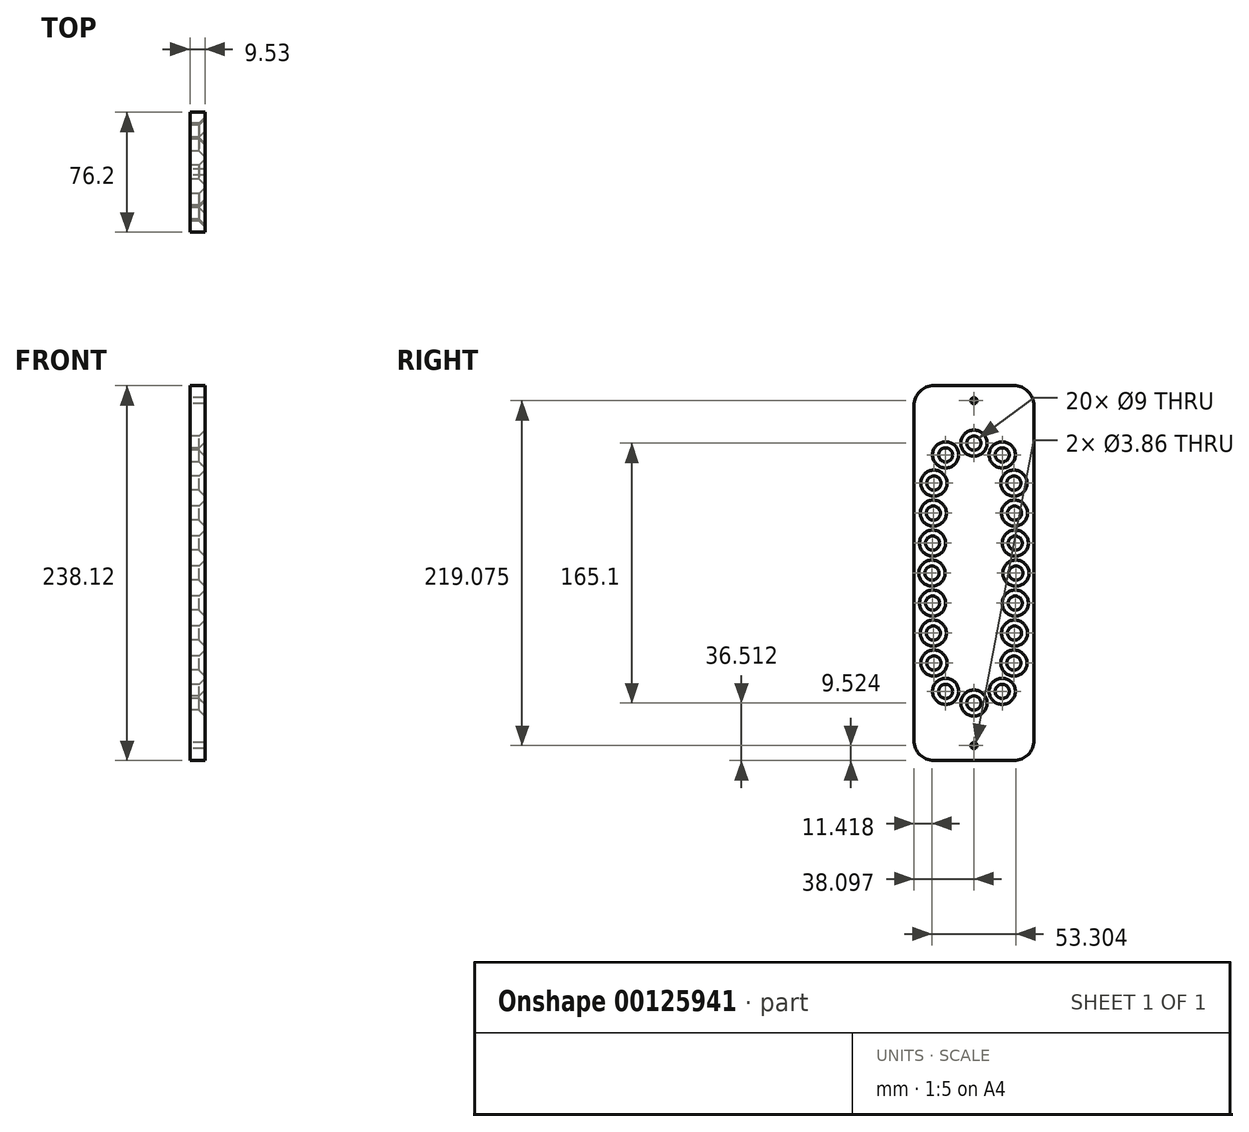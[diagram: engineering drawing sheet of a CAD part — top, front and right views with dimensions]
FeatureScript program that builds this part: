
annotation { "Feature Type Name" : "Feature", "Feature Type Description" : "" }
export const myFeature = defineFeature(function(context is Context, id is Id, definition is map)
    precondition{}
    {
        {
            var Q0;
            Q0=qCreatedBy(makeId("Right.planeOp"),FACE);
            var sketch = newSketch(context, id + "F0", { "sketchPlane" : qUnion([Q0])});
            skLineSegment(sketch, "E0", {"start": v(-38.07, 112.92) * mm, "end": v(-38.07, -99.8) * mm});
            skArc(sketch, "E1", {"start": v(-38.07, 112.92) * mm, "mid": v(-34.35, 121.9) * mm, "end": v(-25.37, 125.62) * mm});
            skLineSegment(sketch, "E2", {"start": v(-25.37, 125.62) * mm, "end": v(0.03, 125.62) * mm});
            skArc(sketch, "E3", {"start": v(-38.07, -99.8) * mm, "mid": v(-34.35, -108.78) * mm, "end": v(-25.37, -112.5) * mm});
            skLineSegment(sketch, "E4", {"start": v(-25.37, -112.5) * mm, "end": v(0.03, -112.5) * mm});
            skLineSegment(sketch, "E5.MirrorCS", {"start": v(25.43, -112.5) * mm, "end": v(0.03, -112.5) * mm});
            skArc(sketch, "E6.MirrorCS", {"start": v(38.13, -99.8) * mm, "mid": v(34.4, -108.78) * mm, "end": v(25.43, -112.5) * mm});
            skLineSegment(sketch, "E7.MirrorCS", {"start": v(25.43, 125.62) * mm, "end": v(0.03, 125.62) * mm});
            skLineSegment(sketch, "E8.MirrorCS", {"start": v(38.13, 112.92) * mm, "end": v(38.13, -99.8) * mm});
            skArc(sketch, "E9.MirrorCS", {"start": v(38.13, 112.92) * mm, "mid": v(34.4, 121.9) * mm, "end": v(25.43, 125.62) * mm});
            skCircle(sketch, "E10", {"center": v(0.03, 116.1) * mm, "radius": 1.93 * mm});
            skCircle(sketch, "E11", {"center": v(0.03, -102.98) * mm, "radius": 1.93 * mm});
            skLineSegment(sketch, "E12", {"start": v(0, -40.43) * mm, "end": v(0, 53.03) * mm, "construction": true});
            skCircle(sketch, "E13", {"center": v(0, 89.11) * mm, "radius": 4.5 * mm});
            skArc(sketch, "E14", {"start": v(-25.4, 63.71) * mm, "mid": v(0, 89.11) * mm, "end": v(25.4, 63.71) * mm, "construction": true});
            skLineSegment(sketch, "E15", {"start": v(-25.4, 63.71) * mm, "end": v(25.4, 63.71) * mm, "construction": true});
            skLineSegment(sketch, "E16", {"start": v(0, 63.71) * mm, "end": v(-17.96, 81.67) * mm, "construction": true});
            skCircle(sketch, "E17", {"center": v(-17.96, 81.67) * mm, "radius": 4.5 * mm});
            skCircle(sketch, "E18", {"center": v(-25.4, 63.71) * mm, "radius": 4.5 * mm});
            skLineSegment(sketch, "E19", {"start": v(-26.65, 6.56) * mm, "end": v(-25.4, 63.71) * mm, "construction": true});
            skCircle(sketch, "E20", {"center": v(-26.65, 6.56) * mm, "radius": 4.5 * mm});
            skCircle(sketch, "E21", {"center": v(-26.23, 25.61) * mm, "radius": 4.5 * mm});
            skCircle(sketch, "E22", {"center": v(-25.82, 44.66) * mm, "radius": 4.5 * mm});
            skCircle(sketch, "E23.MirrorC", {"center": v(26.65, 6.56) * mm, "radius": 4.5 * mm});
            skCircle(sketch, "E24.MirrorC", {"center": v(26.23, 25.61) * mm, "radius": 4.5 * mm});
            skCircle(sketch, "E25.MirrorC", {"center": v(25.82, 44.66) * mm, "radius": 4.5 * mm});
            skCircle(sketch, "E26.MirrorC", {"center": v(25.4, 63.71) * mm, "radius": 4.5 * mm});
            skCircle(sketch, "E27.MirrorC", {"center": v(17.96, 81.67) * mm, "radius": 4.5 * mm});
            skCircle(sketch, "E28.MirrorC", {"center": v(-26.23, -12.49) * mm, "radius": 4.5 * mm});
            skCircle(sketch, "E29.MirrorC", {"center": v(-25.82, -31.54) * mm, "radius": 4.5 * mm});
            skCircle(sketch, "E30.MirrorC", {"center": v(-25.4, -50.59) * mm, "radius": 4.5 * mm});
            skCircle(sketch, "E31.MirrorC", {"center": v(-17.96, -68.55) * mm, "radius": 4.5 * mm});
            skCircle(sketch, "E32.MirrorC", {"center": v(0, -75.99) * mm, "radius": 4.5 * mm});
            skCircle(sketch, "E33.MirrorC", {"center": v(17.96, -68.55) * mm, "radius": 4.5 * mm});
            skCircle(sketch, "E34.MirrorC", {"center": v(25.4, -50.59) * mm, "radius": 4.5 * mm});
            skCircle(sketch, "E35.MirrorC", {"center": v(25.82, -31.54) * mm, "radius": 4.5 * mm});
            skCircle(sketch, "E36.MirrorC", {"center": v(26.23, -12.49) * mm, "radius": 4.5 * mm});
            skSolve(sketch);
        }
        {
            var Q0;
            Q0 = qSketchRegion(id + "F0", true);
            extrude(context, id + "F1", {"entities" : qUnion([Q0]), "depth" : 9.52 * mm});
        }
        {
            var Q0;
            Q0=makeQuery(id+"F1.opExtrude","CAP_EDGE",EDGE,{"disambiguationData":[OSD([sQuery(id+"F0.wireOp",EDGE,"E13")])],"isStart":false});
            var Q1;
            Q1=makeQuery(id+"F1.opExtrude","CAP_EDGE",EDGE,{"disambiguationData":[OSD([sQuery(id+"F0.wireOp",EDGE,"E17")])],"isStart":false});
            var Q2;
            Q2=makeQuery(id+"F1.opExtrude","CAP_EDGE",EDGE,{"disambiguationData":[OSD([sQuery(id+"F0.wireOp",EDGE,"E18")])],"isStart":false});
            var Q3;
            Q3=makeQuery(id+"F1.opExtrude","CAP_EDGE",EDGE,{"disambiguationData":[OSD([sQuery(id+"F0.wireOp",EDGE,"E22")])],"isStart":false});
            var Q4;
            Q4=makeQuery(id+"F1.opExtrude","CAP_EDGE",EDGE,{"disambiguationData":[OSD([sQuery(id+"F0.wireOp",EDGE,"E21")])],"isStart":false});
            var Q5;
            Q5=makeQuery(id+"F1.opExtrude","CAP_EDGE",EDGE,{"disambiguationData":[OSD([sQuery(id+"F0.wireOp",EDGE,"E20")])],"isStart":false});
            var Q6;
            Q6=makeQuery(id+"F1.opExtrude","CAP_EDGE",EDGE,{"disambiguationData":[OSD([sQuery(id+"F0.wireOp",EDGE,"E28.MirrorC")])],"isStart":false});
            var Q7;
            Q7=makeQuery(id+"F1.opExtrude","CAP_EDGE",EDGE,{"disambiguationData":[OSD([sQuery(id+"F0.wireOp",EDGE,"E29.MirrorC")])],"isStart":false});
            var Q8;
            Q8=makeQuery(id+"F1.opExtrude","CAP_EDGE",EDGE,{"disambiguationData":[OSD([sQuery(id+"F0.wireOp",EDGE,"E30.MirrorC")])],"isStart":false});
            var Q9;
            Q9=makeQuery(id+"F1.opExtrude","CAP_EDGE",EDGE,{"disambiguationData":[OSD([sQuery(id+"F0.wireOp",EDGE,"E31.MirrorC")])],"isStart":false});
            var Q10;
            Q10=makeQuery(id+"F1.opExtrude","CAP_EDGE",EDGE,{"disambiguationData":[OSD([sQuery(id+"F0.wireOp",EDGE,"E32.MirrorC")])],"isStart":false});
            var Q11;
            Q11=makeQuery(id+"F1.opExtrude","CAP_EDGE",EDGE,{"disambiguationData":[OSD([sQuery(id+"F0.wireOp",EDGE,"E33.MirrorC")])],"isStart":false});
            var Q12;
            Q12=makeQuery(id+"F1.opExtrude","CAP_EDGE",EDGE,{"disambiguationData":[OSD([sQuery(id+"F0.wireOp",EDGE,"E34.MirrorC")])],"isStart":false});
            var Q13;
            Q13=makeQuery(id+"F1.opExtrude","CAP_EDGE",EDGE,{"disambiguationData":[OSD([sQuery(id+"F0.wireOp",EDGE,"E35.MirrorC")])],"isStart":false});
            var Q14;
            Q14=makeQuery(id+"F1.opExtrude","CAP_EDGE",EDGE,{"disambiguationData":[OSD([sQuery(id+"F0.wireOp",EDGE,"E36.MirrorC")])],"isStart":false});
            var Q15;
            Q15=makeQuery(id+"F1.opExtrude","CAP_EDGE",EDGE,{"disambiguationData":[OSD([sQuery(id+"F0.wireOp",EDGE,"E23.MirrorC")])],"isStart":false});
            var Q16;
            Q16=makeQuery(id+"F1.opExtrude","CAP_EDGE",EDGE,{"disambiguationData":[OSD([sQuery(id+"F0.wireOp",EDGE,"E24.MirrorC")])],"isStart":false});
            var Q17;
            Q17=makeQuery(id+"F1.opExtrude","CAP_EDGE",EDGE,{"disambiguationData":[OSD([sQuery(id+"F0.wireOp",EDGE,"E25.MirrorC")])],"isStart":false});
            var Q18;
            Q18=makeQuery(id+"F1.opExtrude","CAP_EDGE",EDGE,{"disambiguationData":[OSD([sQuery(id+"F0.wireOp",EDGE,"E26.MirrorC")])],"isStart":false});
            var Q19;
            Q19=makeQuery(id+"F1.opExtrude","CAP_EDGE",EDGE,{"disambiguationData":[OSD([sQuery(id+"F0.wireOp",EDGE,"E27.MirrorC")])],"isStart":false});
            chamfer(context, id + "F2", {"entities" : qUnion([Q0, Q1, Q2, Q3, Q4, Q5, Q6, Q7, Q8, Q9, Q10, Q11, Q12, Q13, Q14, Q15, Q16, Q17, Q18, Q19]), "width" : 3.8 * mm, "tangentPropagation" : true});
        }
    });
